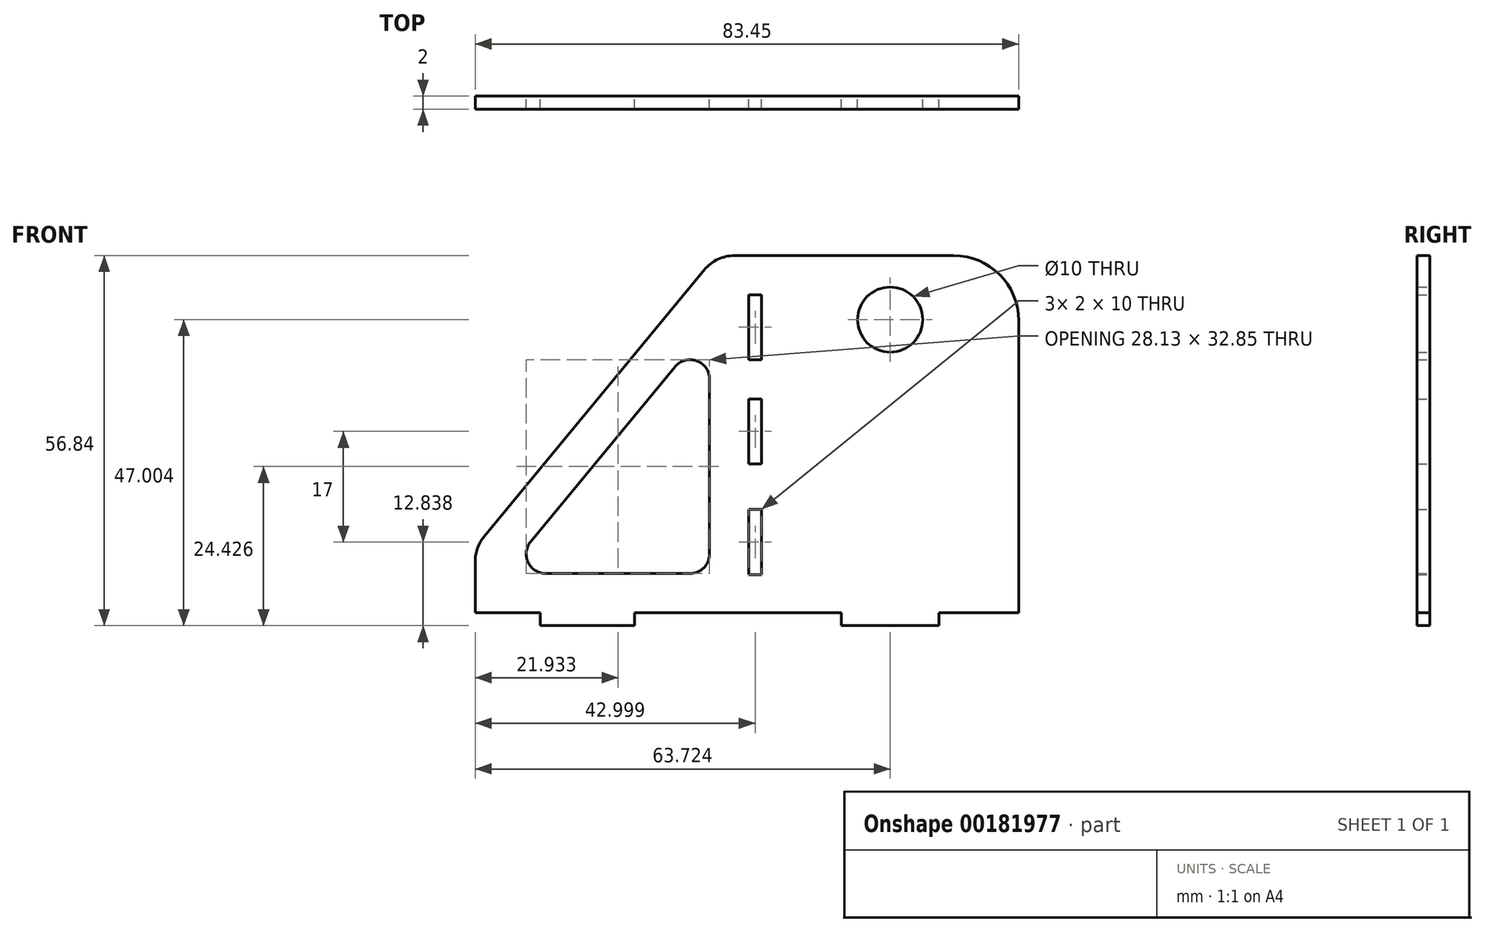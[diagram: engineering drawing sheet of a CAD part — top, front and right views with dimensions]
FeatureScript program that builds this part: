
annotation { "Feature Type Name" : "Feature", "Feature Type Description" : "" }
export const myFeature = defineFeature(function(context is Context, id is Id, definition is map)
    precondition{}
    {
        {
            var Q0;
            Q0=qCreatedBy(makeId("Front.planeOp"),FACE);
            var sketch = newSketch(context, id + "F0", { "sketchPlane" : qUnion([Q0])});
            skLineSegment(sketch, "E0.bottom", {"start": v(-19.58, 33.88) * mm, "end": v(0.14, 33.88) * mm});
            skLineSegment(sketch, "E0.left", {"start": v(-19.58, 27.88) * mm, "end": v(-19.58, 17.88) * mm});
            skLineSegment(sketch, "E1.bottom", {"start": v(-19.58, 33.88) * mm, "end": v(-21.58, 33.88) * mm});
            skLineSegment(sketch, "E1.top", {"start": v(-19.58, -20.96) * mm, "end": v(-21.58, -20.96) * mm});
            skLineSegment(sketch, "E2.bottom", {"start": v(-21.58, 33.88) * mm, "end": v(-23.75, 33.88) * mm});
            skLineSegment(sketch, "E2.top", {"start": v(-21.58, -20.96) * mm, "end": v(-39.08, -20.96) * mm});
            skLineSegment(sketch, "E2.left", {"start": v(-21.58, 27.88) * mm, "end": v(-21.58, 17.88) * mm});
            skLineSegment(sketch, "E2.right", {"start": v(-63.58, -13.11) * mm, "end": v(-63.58, -20.96) * mm});
            skLineSegment(sketch, "E3.top", {"start": v(-7.33, -22.96) * mm, "end": v(0.14, -22.96) * mm});
            skLineSegment(sketch, "E3.left", {"start": v(-7.33, -21.12) * mm, "end": v(-7.33, -22.96) * mm});
            skLineSegment(sketch, "E4.top", {"start": v(-39.08, -22.96) * mm, "end": v(-53.58, -22.96) * mm});
            skLineSegment(sketch, "E4.left", {"start": v(-39.08, -20.96) * mm, "end": v(-39.08, -22.96) * mm});
            skLineSegment(sketch, "E4.right", {"start": v(-53.58, -20.96) * mm, "end": v(-53.58, -22.96) * mm});
            skLineSegment(sketch, "E5", {"start": v(-62.2, -9.3) * mm, "end": v(-28.38, 31.7) * mm});
            skCircle(sketch, "E6", {"center": v(0.14, 24.04) * mm, "radius": 5 * mm});
            skPoint(sketch, "E7.visualSharp", {"position": v(-26.58, 33.88) * mm});
            skArc(sketch, "E7.filletArc", {"start": v(-23.75, 33.88) * mm, "mid": v(-26.31, 33.3) * mm, "end": v(-28.38, 31.7) * mm});
            skPoint(sketch, "E8.visualSharp", {"position": v(-63.58, -10.96) * mm});
            skArc(sketch, "E8.filletArc", {"start": v(-62.2, -9.3) * mm, "mid": v(-63.23, -11.08) * mm, "end": v(-63.58, -13.11) * mm});
            skLineSegment(sketch, "E9", {"start": v(-21.58, 27.88) * mm, "end": v(-19.58, 27.88) * mm});
            skLineSegment(sketch, "E10", {"start": v(-21.58, 17.88) * mm, "end": v(-19.58, 17.88) * mm});
            skLineSegment(sketch, "E11", {"start": v(-21.58, 11.88) * mm, "end": v(-19.58, 11.88) * mm});
            skLineSegment(sketch, "E12", {"start": v(-21.58, -15.12) * mm, "end": v(-19.58, -15.12) * mm});
            skLineSegment(sketch, "E13.trimOffspring", {"start": v(-53.58, -20.96) * mm, "end": v(-63.58, -20.96) * mm});
            skLineSegment(sketch, "E14.trimOffspring", {"start": v(-19.58, 11.88) * mm, "end": v(-19.58, 1.88) * mm});
            skLineSegment(sketch, "E15.trimOffspring", {"start": v(-21.58, 11.88) * mm, "end": v(-21.58, 1.88) * mm});
            skLineSegment(sketch, "E16", {"start": v(-21.58, -5.12) * mm, "end": v(-19.58, -5.12) * mm});
            skLineSegment(sketch, "E17", {"start": v(-21.58, 1.88) * mm, "end": v(-19.58, 1.88) * mm});
            skLineSegment(sketch, "E18", {"start": v(-52.74, -14.96) * mm, "end": v(-30.58, -14.96) * mm});
            skLineSegment(sketch, "E19", {"start": v(-27.58, -11.96) * mm, "end": v(-27.58, 14.9) * mm});
            skLineSegment(sketch, "E20", {"start": v(-32.9, 16.8) * mm, "end": v(-55.05, -10.05) * mm});
            skPoint(sketch, "E21.visualSharp", {"position": v(-27.58, 23.24) * mm});
            skArc(sketch, "E21.filletArc", {"start": v(-27.58, 14.9) * mm, "mid": v(-29.57, 17.71) * mm, "end": v(-32.9, 16.8) * mm});
            skPoint(sketch, "E22.visualSharp", {"position": v(-27.58, -14.96) * mm});
            skArc(sketch, "E22.filletArc", {"start": v(-30.58, -14.96) * mm, "mid": v(-28.46, -14.08) * mm, "end": v(-27.58, -11.96) * mm});
            skArc(sketch, "E23.filletArc", {"start": v(-55.05, -10.05) * mm, "mid": v(-55.45, -13.24) * mm, "end": v(-52.74, -14.96) * mm});
            skLineSegment(sketch, "E24", {"start": v(0.14, 54.4) * mm, "end": v(0.14, -30.42) * mm});
            skLineSegment(sketch, "E25", {"start": v(0.14, -30.42) * mm, "end": v(0.45, -30.42) * mm});
            skPoint(sketch, "E3.right.end.orphan", {"position": v(7.17, -22.96) * mm});
            skLineSegment(sketch, "E26.trimOffspring", {"start": v(-21.58, -5.12) * mm, "end": v(-21.58, -15.12) * mm});
            skLineSegment(sketch, "E27.trimOffspring", {"start": v(-19.58, -5.12) * mm, "end": v(-19.58, -15.12) * mm});
            skLineSegment(sketch, "E28.MirrorCS", {"start": v(7.62, -22.96) * mm, "end": v(0.14, -22.96) * mm});
            skLineSegment(sketch, "E29.MirrorCS", {"start": v(9.87, 33.88) * mm, "end": v(0.14, 33.88) * mm});
            skLineSegment(sketch, "E30.MirrorCS", {"start": v(7.62, -21.12) * mm, "end": v(7.62, -22.96) * mm});
            skLineSegment(sketch, "E31.MirrorCS", {"start": v(19.87, 23.88) * mm, "end": v(19.87, 17.88) * mm});
            skLineSegment(sketch, "E32.MirrorCS", {"start": v(19.87, -5.12) * mm, "end": v(19.87, -15.12) * mm});
            skLineSegment(sketch, "E33.MirrorCS", {"start": v(19.87, 11.88) * mm, "end": v(19.87, 1.88) * mm});
            skLineSegment(sketch, "E34", {"start": v(-63.58, -20.96) * mm, "end": v(-53.58, -20.96) * mm});
            skLineSegment(sketch, "E35", {"start": v(-7.33, -21.12) * mm, "end": v(-7.33, -20.96) * mm});
            skLineSegment(sketch, "E36", {"start": v(7.62, -21.12) * mm, "end": v(7.62, -20.96) * mm});
            skLineSegment(sketch, "E37.trimOffspring", {"start": v(7.62, -20.96) * mm, "end": v(19.87, -20.96) * mm});
            skLineSegment(sketch, "E38.trimOffspring", {"start": v(-39.08, -20.96) * mm, "end": v(-7.33, -20.96) * mm});
            skLineSegment(sketch, "E39", {"start": v(19.87, 23.88) * mm, "end": v(19.87, -20.96) * mm});
            skPoint(sketch, "E40.visualSharp", {"position": v(19.87, 33.88) * mm});
            skArc(sketch, "E40.filletArc", {"start": v(19.87, 23.88) * mm, "mid": v(16.94, 30.95) * mm, "end": v(9.87, 33.88) * mm});
            skSolve(sketch);
        }
        {
            var Q0;
            {var subQ2=sQuery(id+"F0.wireOp",EDGE,"E0.bottom");Q0=makeQuery(id+"F0.imprint","IMPRINT",FACE,{"disambiguationData":[TD([[makeQuery(id+"F0.imprint","IMPRINT",EDGE,{"derivedFrom":subQ2}),-1.0]])]});}
            var Q1;
            {var subQ6=sQuery(id+"F0.wireOp",EDGE,"E28.MirrorCS");Q1=makeQuery(id+"F0.imprint","IMPRINT",FACE,{"disambiguationData":[TD([[makeQuery(id+"F0.imprint","IMPRINT",EDGE,{"derivedFrom":subQ6}),-1.0]])]});}
            extrude(context, id + "F1", {"entities" : qUnion([Q0, Q1]), "depth" : 2 * mm});
        }
    });
